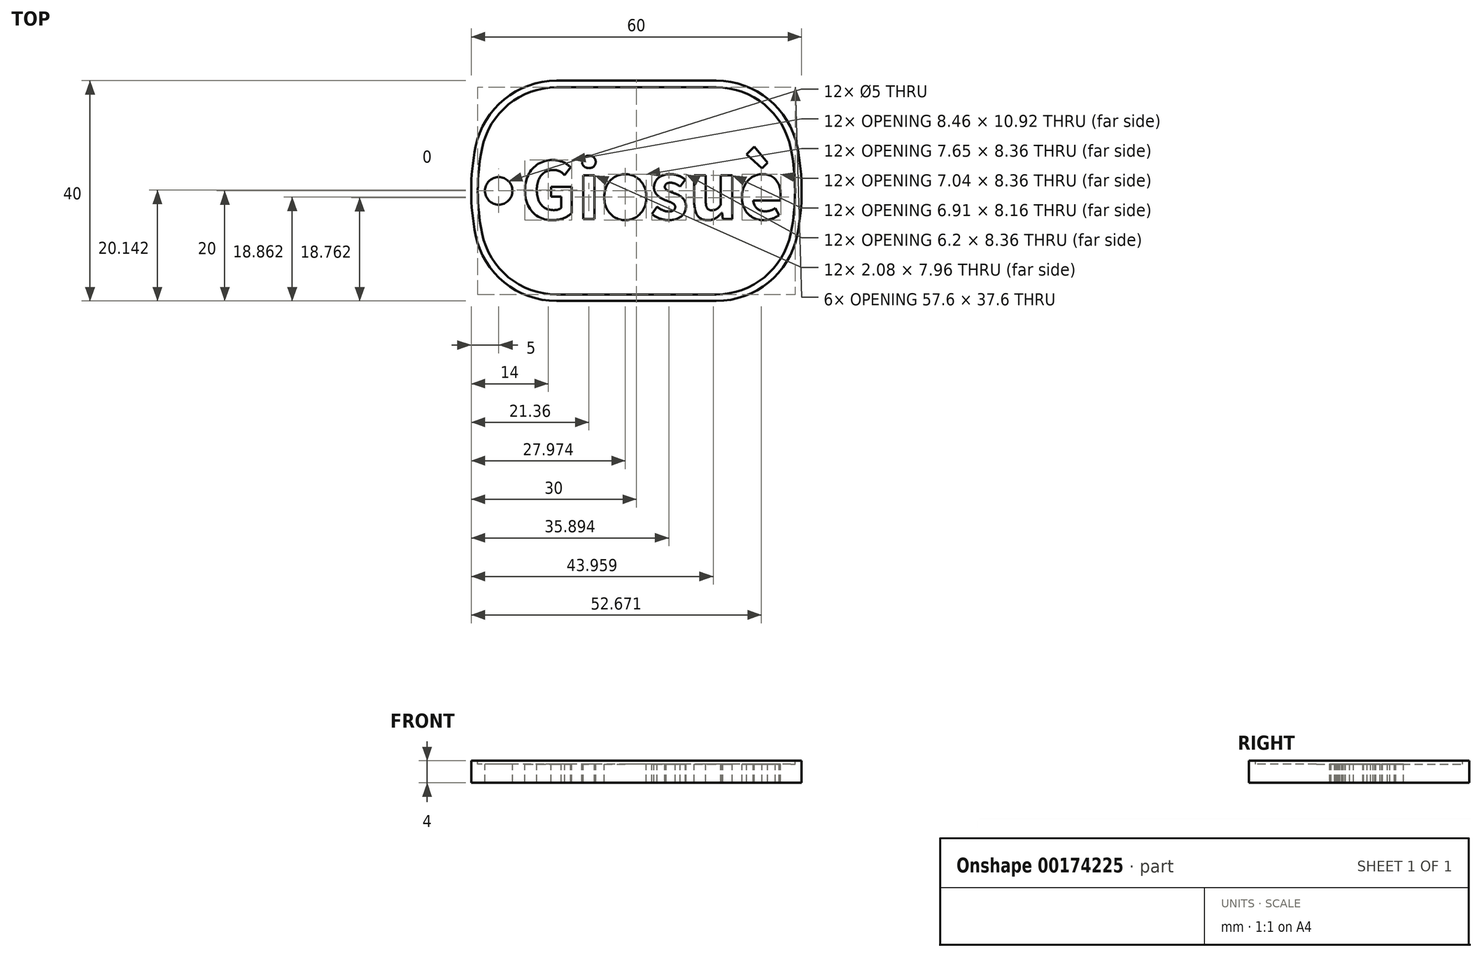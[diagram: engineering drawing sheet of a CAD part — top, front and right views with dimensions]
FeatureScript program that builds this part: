
annotation { "Feature Type Name" : "Feature", "Feature Type Description" : "" }
export const myFeature = defineFeature(function(context is Context, id is Id, definition is map)
    precondition{}
    {
        {
            var Q0;
            Q0=qCreatedBy(makeId("Top.planeOp"),FACE);
            var sketch = newSketch(context, id + "F0", { "sketchPlane" : qUnion([Q0])});
            skLineSegment(sketch, "E0.bottom", {"start": v(30, 20) * mm, "end": v(-30, 20) * mm});
            skLineSegment(sketch, "E0.top", {"start": v(30, -20) * mm, "end": v(-30, -20) * mm});
            skLineSegment(sketch, "E0.left", {"start": v(30, 20) * mm, "end": v(30, -20) * mm});
            skLineSegment(sketch, "E0.right", {"start": v(-30, 20) * mm, "end": v(-30, -20) * mm});
            skPoint(sketch, "E0.middle", {"position": v(0, 0) * mm});
            skArc(sketch, "E1", {"start": v(-24.64, 20) * mm, "mid": v(-30, 0) * mm, "end": v(-24.64, -20) * mm});
            skArc(sketch, "E2.MirrorCS", {"start": v(24.64, 20) * mm, "mid": v(30, 0) * mm, "end": v(24.64, -20) * mm});
            skSolve(sketch);
        }
        {
            var Q0;
            {var subQ0=sQuery(id+"F0.wireOp",EDGE,"E1");var subQ4=sQuery(id+"F0.wireOp",EDGE,"E0.bottom");var subQ5=makeQuery(id+"F0.imprint","INTERSECT",VERTEX,{"derivedFrom":[subQ4,subQ0]});Q0=makeQuery(id+"F0.imprint","IMPRINT",FACE,{"disambiguationData":[TD([[makeQuery(id+"F0.imprint","IMPRINT",EDGE,{"disambiguationData":[TD([[subQ5,1.0]])],"derivedFrom":subQ4}),1.0]])]});}
            extrude(context, id + "F1", {"entities" : qUnion([Q0]), "depth" : 4 * mm});
        }
        {
            var Q0;
            Q0=makeQuery(id+"F1.opExtrude","SWEPT_EDGE",EDGE,{"disambiguationData":[OSD([sQuery(id+"F0.wireOp",EDGE,"E0.top"),sQuery(id+"F0.wireOp",EDGE,"E1")])]});
            var Q1;
            Q1=makeQuery(id+"F1.opExtrude","SWEPT_EDGE",EDGE,{"disambiguationData":[OSD([sQuery(id+"F0.wireOp",EDGE,"E0.top"),sQuery(id+"F0.wireOp",EDGE,"E2.MirrorCS")])]});
            var Q2;
            Q2=makeQuery(id+"F1.opExtrude","SWEPT_EDGE",EDGE,{"disambiguationData":[OSD([sQuery(id+"F0.wireOp",EDGE,"E0.bottom"),sQuery(id+"F0.wireOp",EDGE,"E2.MirrorCS")])]});
            var Q3;
            Q3=makeQuery(id+"F1.opExtrude","SWEPT_EDGE",EDGE,{"disambiguationData":[OSD([sQuery(id+"F0.wireOp",EDGE,"E0.bottom"),sQuery(id+"F0.wireOp",EDGE,"E1")])]});
            fillet(context, id + "F2", {"entities" : qUnion([Q0, Q1, Q2, Q3]), "radius" : 15 * mm, "tangentPropagation" : true, "allowEdgeOverflow" : false});
        }
        {
            var Q0;
            Q0=makeQuery(id+"F1.opExtrude","CAP_FACE",FACE,{"disambiguationData":[OSD([sQuery(id+"F0.wireOp",EDGE,"E0.bottom"),sQuery(id+"F0.wireOp",EDGE,"E0.top"),sQuery(id+"F0.wireOp",EDGE,"E1"),sQuery(id+"F0.wireOp",EDGE,"E2.MirrorCS")])],"isStart":false});
            var sketch = newSketch(context, id + "F3", { "sketchPlane" : qUnion([Q0])});
            skArc(sketch, "E3.0", {"start": v(28.02, 7.76) * mm, "mid": v(23.22, 15.69) * mm, "end": v(14.5, 18.8) * mm});
            skArc(sketch, "E3.1", {"start": v(28.02, 7.76) * mm, "mid": v(28.8, 0) * mm, "end": v(28.02, -7.76) * mm});
            skLineSegment(sketch, "E3.2", {"start": v(14.5, 18.8) * mm, "end": v(-14.5, 18.8) * mm});
            skArc(sketch, "E3.3", {"start": v(14.5, -18.8) * mm, "mid": v(23.22, -15.69) * mm, "end": v(28.02, -7.76) * mm});
            skArc(sketch, "E3.4", {"start": v(-14.5, 18.8) * mm, "mid": v(-23.22, 15.69) * mm, "end": v(-28.02, 7.76) * mm});
            skArc(sketch, "E3.5", {"start": v(-28.02, 7.76) * mm, "mid": v(-28.8, 0) * mm, "end": v(-28.02, -7.76) * mm});
            skArc(sketch, "E3.6", {"start": v(-28.02, -7.76) * mm, "mid": v(-23.22, -15.69) * mm, "end": v(-14.5, -18.8) * mm});
            skLineSegment(sketch, "E3.7", {"start": v(14.5, -18.8) * mm, "end": v(-14.5, -18.8) * mm});
            skSolve(sketch);
        }
        {
            var Q0;
            Q0 = qSketchRegion(id + "F3", true);
            extrude(context, id + "F4", {"entities" : qUnion([Q0]), "operationType" : NewBodyOperationType.REMOVE, "oppositeDirection" : true, "depth" : 0.6 * mm});
        }
        {
            var Q0;
            Q0=makeQuery(id+"F4.boolean.opBoolean","COPY",FACE,{"derivedFrom":makeQuery(id+"F4.opExtrude","CAP_FACE",FACE,{"disambiguationData":[OSD([sQuery(id+"F3.wireOp",EDGE,"E3.0"),sQuery(id+"F3.wireOp",EDGE,"E3.1"),sQuery(id+"F3.wireOp",EDGE,"E3.2"),sQuery(id+"F3.wireOp",EDGE,"E3.3"),sQuery(id+"F3.wireOp",EDGE,"E3.4"),sQuery(id+"F3.wireOp",EDGE,"E3.5"),sQuery(id+"F3.wireOp",EDGE,"E3.6"),sQuery(id+"F3.wireOp",EDGE,"E3.7")])],"isStart":false})});
            var sketch = newSketch(context, id + "F5", { "sketchPlane" : qUnion([Q0])});
            skCircle(sketch, "E4", {"center": v(-25, 0) * mm, "radius": 2.5 * mm});
            skSolve(sketch);
        }
        {
            var Q0;
            Q0=makeQuery(id+"F5.imprint","IMPRINT",FACE,{"disambiguationData":[TD([[makeQuery(id+"F5.imprint","IMPRINT",EDGE,{"derivedFrom":sQuery(id+"F5.wireOp",EDGE,"E4")}),1.0]])]});
            extrude(context, id + "F6", {"entities" : qUnion([Q0]), "operationType" : NewBodyOperationType.REMOVE, "oppositeDirection" : true, "depth" : 25 * mm});
        }
        {
            var Q0;
            Q0=makeQuery(id+"F4.boolean.opBoolean","COPY",FACE,{"derivedFrom":makeQuery(id+"F4.opExtrude","CAP_FACE",FACE,{"disambiguationData":[OSD([sQuery(id+"F3.wireOp",EDGE,"E3.0"),sQuery(id+"F3.wireOp",EDGE,"E3.1"),sQuery(id+"F3.wireOp",EDGE,"E3.2"),sQuery(id+"F3.wireOp",EDGE,"E3.3"),sQuery(id+"F3.wireOp",EDGE,"E3.4"),sQuery(id+"F3.wireOp",EDGE,"E3.5"),sQuery(id+"F3.wireOp",EDGE,"E3.6"),sQuery(id+"F3.wireOp",EDGE,"E3.7")])],"isStart":false})});
            var sketch = newSketch(context, id + "F7", { "sketchPlane" : qUnion([Q0])});
            skText(sketch, "E5", { "text": "Giosuè", "fontName": "NotoSansCJKjp-Bold.otf"});
            skLineSegment(sketch, "E6", {"start": v(-21, 0) * mm, "end": v(27, 0) * mm, "construction": true});
            const initialGuessF7  = {"E5": [-0.021, -0.00512, 1, 0, 0.01024]};
            skSetInitialGuess(sketch, initialGuessF7);
            skSolve(sketch);
        }
        {
            var Q0;
            Q0 = qSketchRegion(id + "F7", true);
            var Q1;
            Q1=makeQuery(id+"F7.imprint","IMPRINT",FACE,{"disambiguationData":[TD([[makeQuery(id+"F7.imprint","IMPRINT",EDGE,{"derivedFrom":sQuery(id+"F7.wireOp",EDGE,"E5.sketch_text.stroke-26")}),-1.0]])]});
            var Q2;
            Q2=makeQuery(id+"F7.imprint","IMPRINT",FACE,{"disambiguationData":[TD([[makeQuery(id+"F7.imprint","IMPRINT",EDGE,{"derivedFrom":sQuery(id+"F7.wireOp",EDGE,"E5.sketch_text.stroke-66")}),-1.0]])]});
            extrude(context, id + "F8", {"entities" : qUnion([Q0, Q1, Q2]), "operationType" : NewBodyOperationType.REMOVE, "oppositeDirection" : true, "depth" : 25 * mm});
        }
    });
